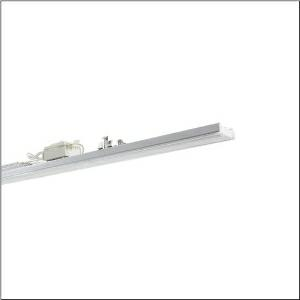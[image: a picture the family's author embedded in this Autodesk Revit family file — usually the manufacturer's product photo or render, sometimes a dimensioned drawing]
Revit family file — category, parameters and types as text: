
# Revit family: licross_r__11_recessed_ho_51tl12dn455m_18c8
name_source: partatom
category: Lighting Fixtures
units: mm (PartAtom-declared; Revit-internal decimal feet)

## family parameters
Cut with Voids When Loaded = No
Host = Face
Light Source = No
Part Type = Normal
Room Calculation Point = No
Round Connector Dimension = Use Diameter
Shared = No

## types (1)
- --- (1 x LED, 5960 lm, 30.6 W, 4000K)
    Apparent Load = 31 VA
    CIE Flux Codes = 66 91 98 100 100
    Color Rendering = 80
    Color Temperature = 4000K
    Default Elevation = 1800 mm
    Description = Licross® 11 Recessed HO, luminaire insert, of sheet steel, coil coated, white, length: 1.500mm, width: 66mm, height: 67mm, LED rated luminous flux: 5.960lm, light colour: 840, control gear: DALI 2, with plug, 5-pole, with phase selection, mains connection: 220..240V, AC, 50/60Hz, rated input power: 31W, internal wiring halogen-free, primary optical cover: cover, of PMMA, light emission: direct distribution, primary light characteristic: symmetric, protection rating (complete): IP40, insulation class (complete): insulation class I (protective earthing), certification: CE, ENEC, VDE, UKCA, protection symbol: D if used in an environment without relevant dust loads with corresponding accessories, impact resistance: IK06, permissible ambient temperature for indoor applications: -25..+45°C, corresponds to IFS (International Featured Standards) requirements for safety and quality in the food industry, reducing of maximum allowable ambient temperature of 5°C with ceiling mounting, LABS conformity tested according to VDMA 24364:2018-05, packaging unit: 1 piece
    Height = 58 mm
    Lamp = 1 x LED
    Lamp Light Flux = 5960 lm
    Lamp Power = 30.6 W
    Lamp count = 1
    Length = 1500 mm
    Luminous efficacy = 195 lm/W
    Manufacturer = Siteco
    ModVariant = No
    Model = 51TL12DN455M
    Mounting Place = Ceiling
    Mounting Type = Pendant
    Number of Poles = 1
    OnlyDefault = Yes
    Power Factor = 1
    Product Name = Licross® 11 Recessed HO
    Product group = luminaire insert | ceiling pendant
    ProductGroupID = 902
    Protection Class = Protection class I
    Protection Degree = IP 40
    RLX_Detail_Level = 1
    RLX_Emergency_Light_Flux = 0 lm
    RLX_Emergency_Type = 0
    RLX_Emergency_Type_DB = No
    RlxData = <blob elided: 24313 chars, md5=596ba2d6>
    Socket = socket
    Standby Power = 0 W
    System Light Flux = 5960 lm
    System Power = 31 W
    Type Comments = factory setting: luminous flux: 100 % | dim-lin: 254 | 212 mA
    Type Image = l_1296930.jpg
    URL = http://relux.com
    VarID = @adj_121001
    Voltage = 0 V
    Weight = 0.00 kg
    Width = 66 mm

## geometry (parser evidence)
native form markers: Blend x4, Sweep x13
no freeform markers — native parametric forms only
